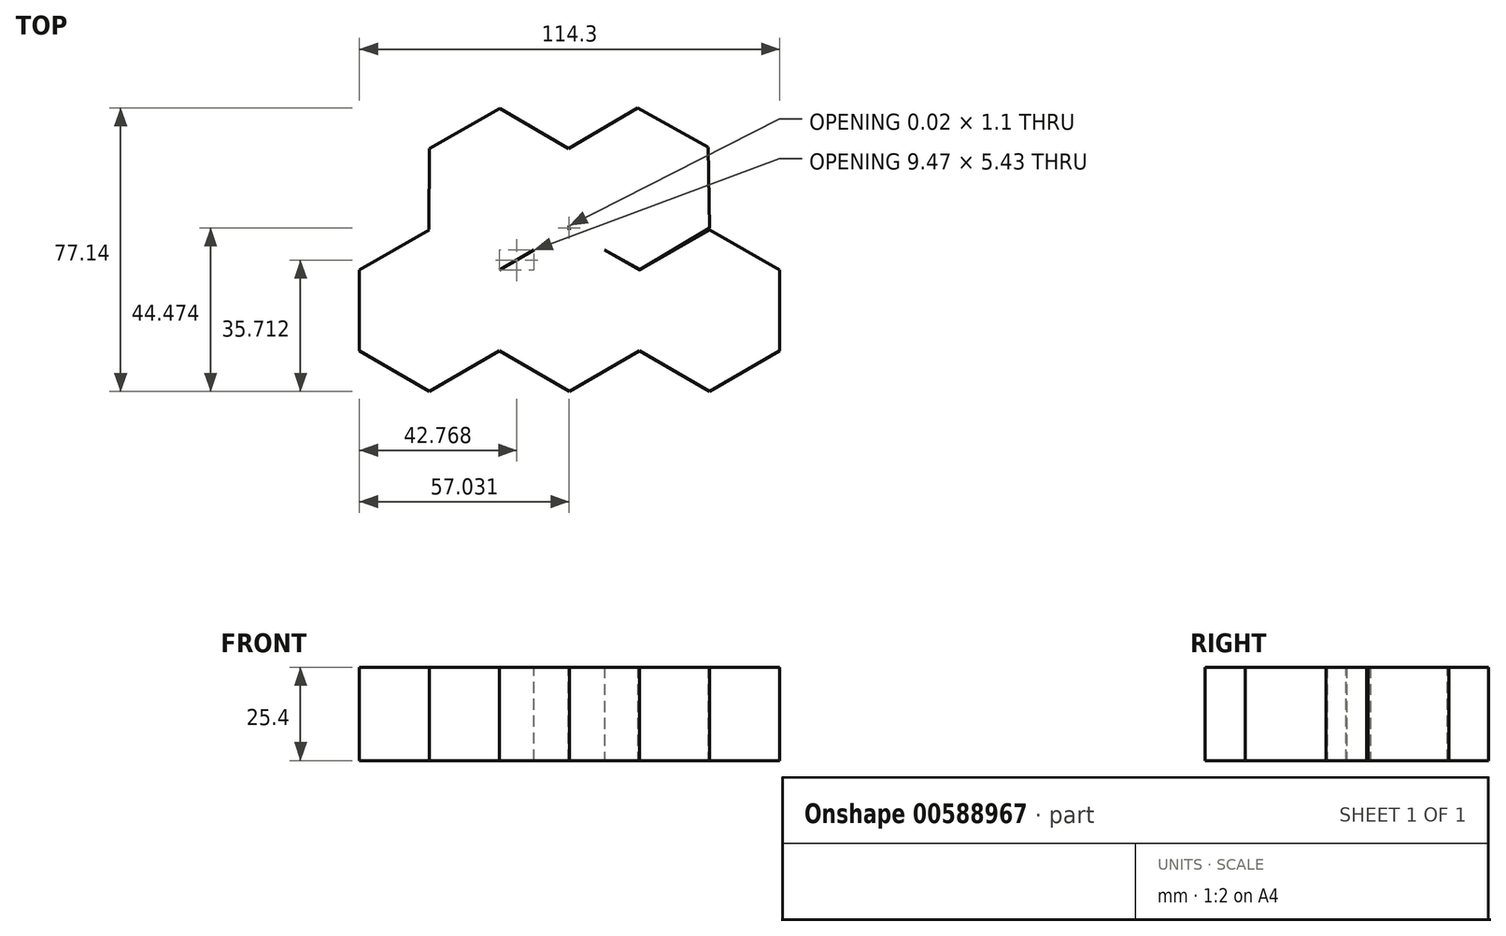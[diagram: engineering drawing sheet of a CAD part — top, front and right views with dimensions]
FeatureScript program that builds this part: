
annotation { "Feature Type Name" : "Feature", "Feature Type Description" : "" }
export const myFeature = defineFeature(function(context is Context, id is Id, definition is map)
    precondition{}
    {
        {
            var Q0;
            Q0=qCreatedBy(makeId("Top.planeOp"),FACE);
            var sketch = newSketch(context, id + "F0", { "sketchPlane" : qUnion([Q0])});
            skCircle(sketch, "E0.cCircle", {"center": v(0, 0) * mm, "radius": 19.05 * mm, "construction": true});
            skLineSegment(sketch, "E0.0", {"start": v(19.05, 11) * mm, "end": v(19.05, -11) * mm});
            skLineSegment(sketch, "E0.1", {"start": v(19.05, -11) * mm, "end": v(0, -22) * mm});
            skLineSegment(sketch, "E0.2", {"start": v(0, -22) * mm, "end": v(-19.05, -11) * mm});
            skLineSegment(sketch, "E0.3", {"start": v(-19.05, -11) * mm, "end": v(-19.05, 11) * mm});
            skLineSegment(sketch, "E0.4", {"start": v(-19.05, 11) * mm, "end": v(0, 22) * mm});
            skLineSegment(sketch, "E0.5", {"start": v(0, 22) * mm, "end": v(19.05, 11) * mm});
            skPoint(sketch, "E0.0.midPoint", {"position": v(19.05, 0) * mm});
            skSolve(sketch);
        }
        {
            var Q0;
            Q0=makeQuery(id+"F0.imprint","IMPRINT",FACE,{"disambiguationData":[TD([[makeQuery(id+"F0.imprint","IMPRINT",EDGE,{"derivedFrom":sQuery(id+"F0.wireOp",EDGE,"E0.0")}),-1.0]])]});
            extrude(context, id + "F1", {"entities" : qUnion([Q0]), "depth" : 25.4 * mm, "offsetDistance" : 25.4 * mm});
        }
        {
            var Q0;
            Q0=qCreatedBy(makeId("Top.planeOp"),FACE);
            var sketch = newSketch(context, id + "F2", { "sketchPlane" : qUnion([Q0])});
            skCircle(sketch, "E1.cCircle", {"center": v(38.1, 0) * mm, "radius": 19.05 * mm, "construction": true});
            skLineSegment(sketch, "E1.0", {"start": v(19.05, -11) * mm, "end": v(19.05, 11) * mm});
            skLineSegment(sketch, "E1.1", {"start": v(19.05, 11) * mm, "end": v(38.1, 22) * mm});
            skLineSegment(sketch, "E1.2", {"start": v(38.1, 22) * mm, "end": v(57.15, 11) * mm});
            skLineSegment(sketch, "E1.3", {"start": v(57.15, 11) * mm, "end": v(57.15, -11) * mm});
            skLineSegment(sketch, "E1.4", {"start": v(57.15, -11) * mm, "end": v(38.1, -22) * mm});
            skLineSegment(sketch, "E1.5", {"start": v(38.1, -22) * mm, "end": v(19.05, -11) * mm});
            skPoint(sketch, "E1.0.midPoint", {"position": v(19.05, 0) * mm});
            skSolve(sketch);
        }
        {
            var Q0;
            Q0=qCreatedBy(makeId("Top.planeOp"),FACE);
            var sketch = newSketch(context, id + "F3", { "sketchPlane" : qUnion([Q0])});
            skCircle(sketch, "E2.cCircle", {"center": v(18.8, 33.14) * mm, "radius": 19.05 * mm, "construction": true});
            skLineSegment(sketch, "E2.0", {"start": v(37.99, 22.4) * mm, "end": v(19.09, 11.15) * mm});
            skLineSegment(sketch, "E2.1", {"start": v(19.09, 11.15) * mm, "end": v(-0.1, 21.9) * mm});
            skLineSegment(sketch, "E2.2", {"start": v(-0.1, 21.9) * mm, "end": v(-0.4, 43.89) * mm});
            skLineSegment(sketch, "E2.3", {"start": v(-0.4, 43.89) * mm, "end": v(18.5, 55.14) * mm});
            skLineSegment(sketch, "E2.4", {"start": v(18.5, 55.14) * mm, "end": v(37.7, 44.4) * mm});
            skLineSegment(sketch, "E2.5", {"start": v(37.7, 44.4) * mm, "end": v(37.99, 22.4) * mm});
            skPoint(sketch, "E2.0.midPoint", {"position": v(28.54, 16.77) * mm});
            skSolve(sketch);
        }
        {
            var Q0;
            Q0=qCreatedBy(makeId("Top.planeOp"),FACE);
            var sketch = newSketch(context, id + "F4", { "sketchPlane" : qUnion([Q0])});
            skCircle(sketch, "E3.cCircle", {"center": v(-38.1, 0) * mm, "radius": 19.05 * mm, "construction": true});
            skLineSegment(sketch, "E3.0", {"start": v(-19.05, 11) * mm, "end": v(-19.05, -11) * mm});
            skLineSegment(sketch, "E3.1", {"start": v(-19.05, -11) * mm, "end": v(-38.1, -22) * mm});
            skLineSegment(sketch, "E3.2", {"start": v(-38.1, -22) * mm, "end": v(-57.15, -11) * mm});
            skLineSegment(sketch, "E3.3", {"start": v(-57.15, -11) * mm, "end": v(-57.15, 11) * mm});
            skLineSegment(sketch, "E3.4", {"start": v(-57.15, 11) * mm, "end": v(-38.1, 22) * mm});
            skLineSegment(sketch, "E3.5", {"start": v(-38.1, 22) * mm, "end": v(-19.05, 11) * mm});
            skPoint(sketch, "E3.0.midPoint", {"position": v(-19.05, 0) * mm});
            skSolve(sketch);
        }
        {
            var Q0;
            Q0=qCreatedBy(makeId("Top.planeOp"),FACE);
            var sketch = newSketch(context, id + "F5", { "sketchPlane" : qUnion([Q0])});
            skCircle(sketch, "E4.cCircle", {"center": v(-19.11, 32.96) * mm, "radius": 19.05 * mm, "construction": true});
            skLineSegment(sketch, "E4.0", {"start": v(-0.13, 21.85) * mm, "end": v(-19.24, 10.96) * mm});
            skLineSegment(sketch, "E4.1", {"start": v(-19.24, 10.96) * mm, "end": v(-38.23, 22.07) * mm});
            skLineSegment(sketch, "E4.2", {"start": v(-38.23, 22.07) * mm, "end": v(-38.1, 44.07) * mm});
            skLineSegment(sketch, "E4.3", {"start": v(-38.1, 44.07) * mm, "end": v(-18.98, 54.95) * mm});
            skLineSegment(sketch, "E4.4", {"start": v(-18.98, 54.95) * mm, "end": v(0, 43.84) * mm});
            skLineSegment(sketch, "E4.5", {"start": v(0, 43.84) * mm, "end": v(-0.13, 21.85) * mm});
            skPoint(sketch, "E4.0.midPoint", {"position": v(-9.69, 16.4) * mm});
            skSolve(sketch);
        }
        {
            var Q0;
            Q0=makeQuery(id+"F5.imprint","IMPRINT",FACE,{"disambiguationData":[TD([[makeQuery(id+"F5.imprint","IMPRINT",EDGE,{"derivedFrom":sQuery(id+"F5.wireOp",EDGE,"E4.0")}),-1.0]])]});
            extrude(context, id + "F6", {"entities" : qUnion([Q0]), "operationType" : NewBodyOperationType.ADD, "depth" : 25.4 * mm, "offsetDistance" : 25.4 * mm});
        }
        {
            var Q0;
            Q0=makeQuery(id+"F4.imprint","IMPRINT",FACE,{"disambiguationData":[TD([[makeQuery(id+"F4.imprint","IMPRINT",EDGE,{"derivedFrom":sQuery(id+"F4.wireOp",EDGE,"E3.0")}),-1.0]])]});
            extrude(context, id + "F7", {"entities" : qUnion([Q0]), "operationType" : NewBodyOperationType.ADD, "depth" : 25.4 * mm, "offsetDistance" : 25.4 * mm});
        }
        {
            var Q0;
            Q0=makeQuery(id+"F3.imprint","IMPRINT",FACE,{"disambiguationData":[TD([[makeQuery(id+"F3.imprint","IMPRINT",EDGE,{"derivedFrom":sQuery(id+"F3.wireOp",EDGE,"E2.0")}),-1.0]])]});
            extrude(context, id + "F8", {"entities" : qUnion([Q0]), "operationType" : NewBodyOperationType.ADD, "depth" : 25.4 * mm, "offsetDistance" : 25.4 * mm});
        }
        {
            var Q0;
            Q0=makeQuery(id+"F2.imprint","IMPRINT",FACE,{"disambiguationData":[TD([[makeQuery(id+"F2.imprint","IMPRINT",EDGE,{"derivedFrom":sQuery(id+"F2.wireOp",EDGE,"E1.0")}),-1.0]])]});
            extrude(context, id + "F9", {"entities" : qUnion([Q0]), "operationType" : NewBodyOperationType.ADD, "depth" : 25.4 * mm, "offsetDistance" : 25.4 * mm});
        }
    });
